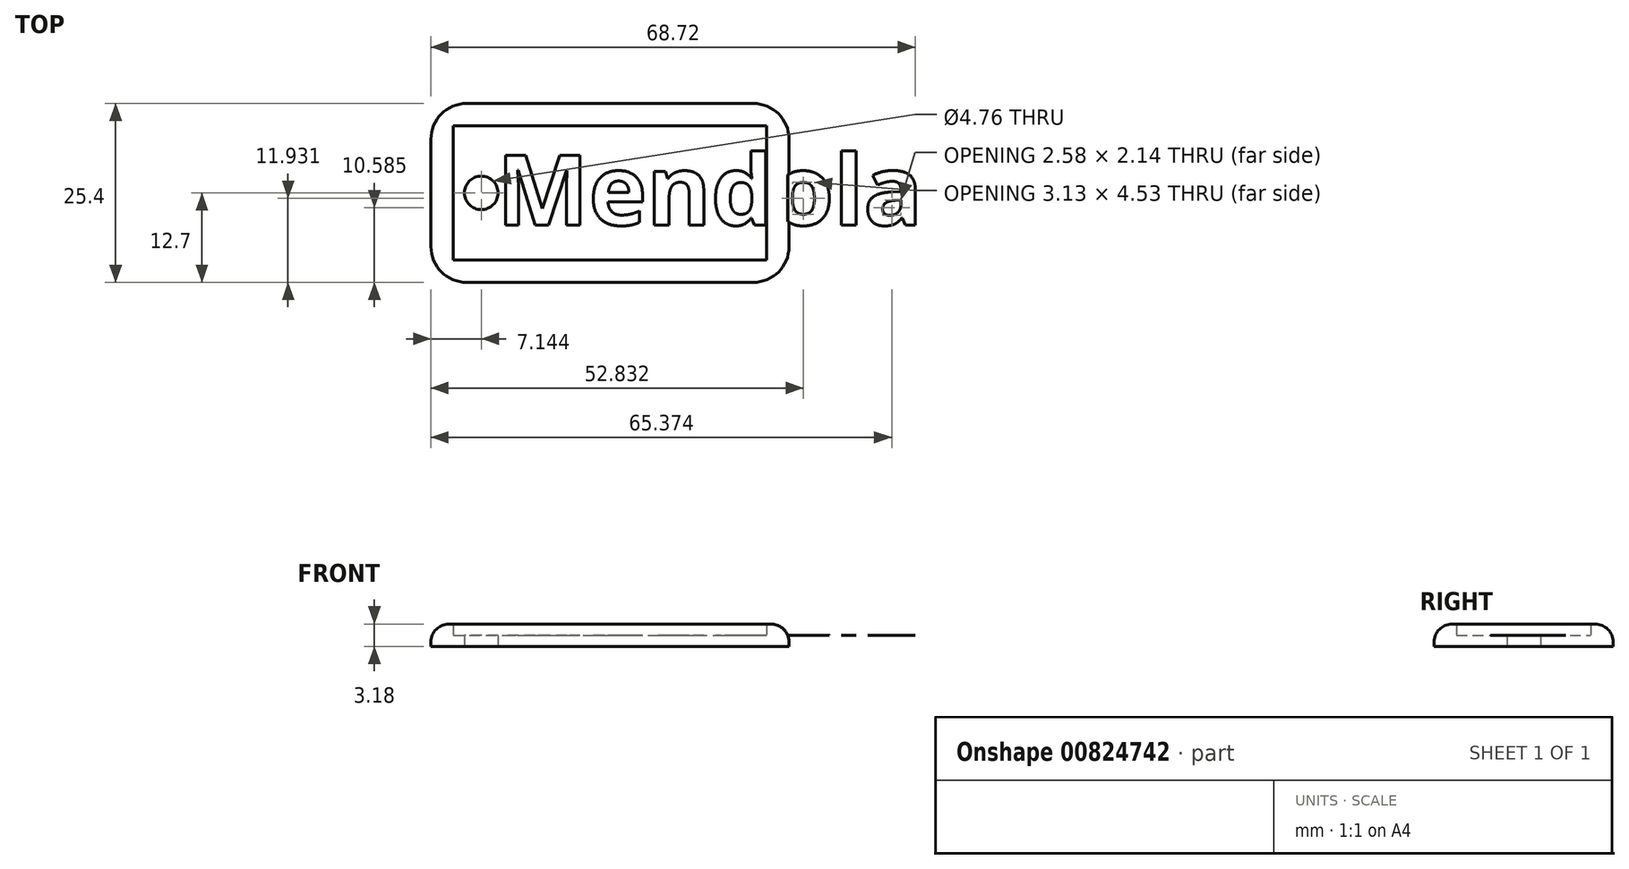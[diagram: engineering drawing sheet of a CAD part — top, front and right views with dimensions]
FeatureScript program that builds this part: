
annotation { "Feature Type Name" : "Feature", "Feature Type Description" : "" }
export const myFeature = defineFeature(function(context is Context, id is Id, definition is map)
    precondition{}
    {
        {
            var Q0;
            Q0=qCreatedBy(makeId("Top.planeOp"),FACE);
            var sketch = newSketch(context, id + "F0", { "sketchPlane" : qUnion([Q0])});
            skLineSegment(sketch, "E0.bottom", {"start": v(0, 0) * mm, "end": v(50.8, 0) * mm});
            skLineSegment(sketch, "E0.top", {"start": v(0, 25.4) * mm, "end": v(50.8, 25.4) * mm});
            skLineSegment(sketch, "E0.left", {"start": v(0, 0) * mm, "end": v(0, 25.4) * mm});
            skLineSegment(sketch, "E0.right", {"start": v(50.8, 0) * mm, "end": v(50.8, 25.4) * mm});
            skCircle(sketch, "E1", {"center": v(7.14, 12.7) * mm, "radius": 2.38 * mm});
            skPoint(sketch, "E1.centerSnap0", {"position": v(0, 12.7) * mm});
            skLineSegment(sketch, "E2.0", {"start": v(3.18, 22.23) * mm, "end": v(47.62, 22.23) * mm});
            skLineSegment(sketch, "E2.1", {"start": v(3.18, 3.18) * mm, "end": v(3.17, 22.23) * mm});
            skLineSegment(sketch, "E2.2", {"start": v(3.18, 3.18) * mm, "end": v(47.62, 3.18) * mm});
            skLineSegment(sketch, "E2.3", {"start": v(47.62, 3.18) * mm, "end": v(47.62, 22.23) * mm});
            skSolve(sketch);
        }
        {
            var Q0;
            Q0=makeQuery(id+"F0.imprint","IMPRINT",FACE,{"disambiguationData":[TD([[makeQuery(id+"F0.imprint","IMPRINT",EDGE,{"derivedFrom":sQuery(id+"F0.wireOp",EDGE,"E1")}),-1.0]])]});
            extrude(context, id + "F1", {"entities" : qUnion([Q0]), "depth" : 1.59 * mm, "offsetDistance" : 25.4 * mm});
        }
        {
            var Q0;
            Q0 = qSketchRegion(id + "F0", true);
            var Q1;
            Q1 = qSketchRegion(id + "F6", true);
            extrude(context, id + "F2", {"entities" : qUnion([Q0, Q1]), "operationType" : NewBodyOperationType.ADD, "depth" : 3.17 * mm, "offsetDistance" : 25.4 * mm});
        }
        {
            var Q0;
            Q0=makeQuery(id+"F2.opExtrude","SWEPT_EDGE",EDGE,{"disambiguationData":[OSD([sQuery(id+"F0.wireOp",EDGE,"E0.bottom"),sQuery(id+"F0.wireOp",EDGE,"E0.right")])]});
            var Q1;
            Q1=makeQuery(id+"F2.opExtrude","SWEPT_EDGE",EDGE,{"disambiguationData":[OSD([sQuery(id+"F0.wireOp",EDGE,"E0.top"),sQuery(id+"F0.wireOp",EDGE,"E0.right")])]});
            var Q2;
            Q2=makeQuery(id+"F2.opExtrude","SWEPT_EDGE",EDGE,{"disambiguationData":[OSD([sQuery(id+"F0.wireOp",EDGE,"E0.top"),sQuery(id+"F0.wireOp",EDGE,"E0.left")])]});
            var Q3;
            Q3=makeQuery(id+"F2.opExtrude","SWEPT_EDGE",EDGE,{"disambiguationData":[OSD([sQuery(id+"F0.wireOp",EDGE,"E0.bottom"),sQuery(id+"F0.wireOp",EDGE,"E0.left")])]});
            fillet(context, id + "F3", {"entities" : qUnion([Q0, Q1, Q2, Q3]), "radius" : 5.08 * mm, "tangentPropagation" : true, "allowEdgeOverflow" : false});
        }
        {
            var Q0;
            Q0=makeQuery(id+"F2.opExtrude","CAP_EDGE",EDGE,{"disambiguationData":[OSD([sQuery(id+"F0.wireOp",EDGE,"E0.bottom")])],"isStart":false});
            fillet(context, id + "F4", {"entities" : qUnion([Q0]), "radius" : 2.54 * mm, "tangentPropagation" : true, "allowEdgeOverflow" : false});
        }
        {
            var Q0;
            Q0=makeQuery(id+"F1.opExtrude","CAP_FACE",FACE,{"disambiguationData":[OSD([sQuery(id+"F0.wireOp",EDGE,"E1"),sQuery(id+"F0.wireOp",EDGE,"E2.0"),sQuery(id+"F0.wireOp",EDGE,"E2.1"),sQuery(id+"F0.wireOp",EDGE,"E2.2"),sQuery(id+"F0.wireOp",EDGE,"E2.3")])],"isStart":false});
            var sketch = newSketch(context, id + "F5", { "sketchPlane" : qUnion([Q0])});
            skText(sketch, "E3", { "text": "Mendola", "fontName": "OpenSans-Bold.ttf"});
            const initialGuessF5  = {"E3": [0.00932, 0.00814, 1, 0, 0.01]};
            skSetInitialGuess(sketch, initialGuessF5);
            skSolve(sketch);
        }
        {
            var Q0;
            Q0=makeQuery(id+"F5.imprint","IMPRINT",FACE,{"disambiguationData":[TD([[makeQuery(id+"F5.imprint","IMPRINT",EDGE,{"derivedFrom":sQuery(id+"F5.wireOp",EDGE,"E3.sketch_text.stroke-7")}),1.0]])]});
            var sketch = newSketch(context, id + "F6", { "sketchPlane" : qUnion([Q0])});
            skSolve(sketch);
        }
        {
            var Q0;
            Q0 = qSketchRegion(id + "F5", true);
            extrude(context, id + "F7", {"entities" : qUnion([Q0]), "operationType" : NewBodyOperationType.ADD, "depth" : 1 / 1625.6 * mm, "offsetDistance" : 25.4 * mm});
        }
    });
